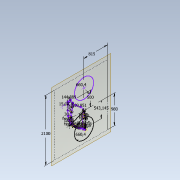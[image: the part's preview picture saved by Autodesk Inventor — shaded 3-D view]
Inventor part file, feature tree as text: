
AUTODESK INVENTOR PART (.ipt)
format: ipt  version: 2021 (Build 250183000, 183)  size: 1,081,856 bytes
history: native  units: mm
features: sketch x4, plane x2, other x2
ambient origin geometry x8: Origin, YZ Plane, XZ Plane, XY Plane, X Axis, Y Axis, Z Axis, Center Point
feature tree (8):
  sketch  "Boceto 3D1"  dims[d3=509.95112mm]
  sketch  "Boceto 3D2"  dims[d100=144.888874mm]
  sketch  "Boceto 3D3"  dims[d175=52.5mm d176=52.5mm d177=52.5mm d178=52.5mm d179=52.5mm d180=30.0mm d208=6.0mm d210=52.5mm d211=35.0mm d212=65.0mm d213=52.5mm d214=52.5mm d216=660.4mm d217=660.4mm d234=980.0mm d236=2100.0mm d237=815.0mm d277=70.0mm d369=32.0mm]
  plane  "Plano de trabajo1"
  other  "Punto de trabajo1"
  sketch  "Boceto2"  dims[d154=500.0mm]
  plane  "Plano de trabajo2"
  other  "Imagen2"
